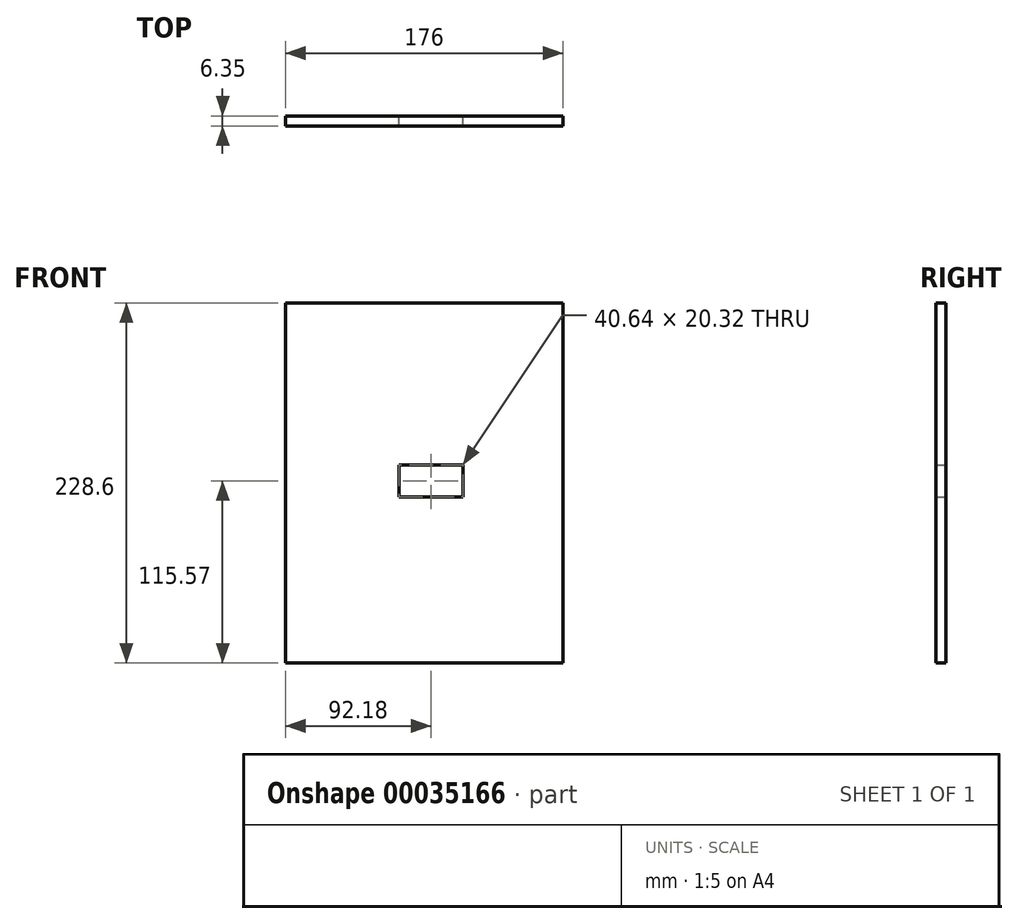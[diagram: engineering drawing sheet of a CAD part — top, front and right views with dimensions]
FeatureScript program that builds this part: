
annotation { "Feature Type Name" : "Feature", "Feature Type Description" : "" }
export const myFeature = defineFeature(function(context is Context, id is Id, definition is map)
    precondition{}
    {
        {
            var Q0;
            Q0=qCreatedBy(makeId("Front.planeOp"),FACE);
            var sketch = newSketch(context, id + "F0", { "sketchPlane" : qUnion([Q0])});
            skLineSegment(sketch, "E0.bottom", {"start": v(-74.43, 123.2) * mm, "end": v(101.57, 123.2) * mm});
            skLineSegment(sketch, "E0.top", {"start": v(-74.43, -105.41) * mm, "end": v(101.57, -105.41) * mm});
            skLineSegment(sketch, "E0.left", {"start": v(-74.43, 123.2) * mm, "end": v(-74.43, -105.41) * mm});
            skLineSegment(sketch, "E0.right", {"start": v(101.57, 123.2) * mm, "end": v(101.57, -105.41) * mm});
            skLineSegment(sketch, "E1.bottom", {"start": v(-2.57, 20.32) * mm, "end": v(38.07, 20.32) * mm});
            skLineSegment(sketch, "E1.top", {"start": v(-2.57, 0) * mm, "end": v(38.07, 0) * mm});
            skLineSegment(sketch, "E1.left", {"start": v(-2.57, 20.32) * mm, "end": v(-2.57, 0) * mm});
            skLineSegment(sketch, "E1.right", {"start": v(38.07, 20.32) * mm, "end": v(38.07, 0) * mm});
            skSolve(sketch);
        }
        {
            var Q0;
            Q0=makeQuery(id+"F0.imprint","IMPRINT",FACE,{"disambiguationData":[TD([[makeQuery(id+"F0.imprint","IMPRINT",EDGE,{"derivedFrom":sQuery(id+"F0.wireOp",EDGE,"E0.bottom")}),-1.0]])]});
            extrude(context, id + "F1", {"entities" : qUnion([Q0]), "depth" : 6.35 * mm});
        }
    });
